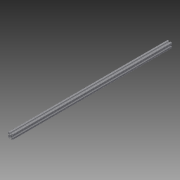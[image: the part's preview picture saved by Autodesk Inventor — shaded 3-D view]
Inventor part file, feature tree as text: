
AUTODESK INVENTOR PART (.ipt)
format: ipt  version: 2013 (Build 170138000, 138)  size: 287,744 bytes
history: native  units: in
note: dims shown in document units (in); Inventor stores cm internally (conversion verified against a paired STEP export)
features: extrude x1, sketch x1
ambient origin geometry x8: Origin, YZ Plane, XZ Plane, XY Plane, X Axis, Y Axis, Z Axis, Center Point
bodies: Solid1 (feature_tree)
feature tree (2):
  extrude  "Extrusion1"  [1 undecoded]
  sketch  "Sketch1"  dims[d0=49.0in d1=0.0in]
note: 1 required parameter value undecoded (feature->parameter linkage not recoverable at this tier; creation-order binding heuristic only, values carry confidence <= 0.55)
